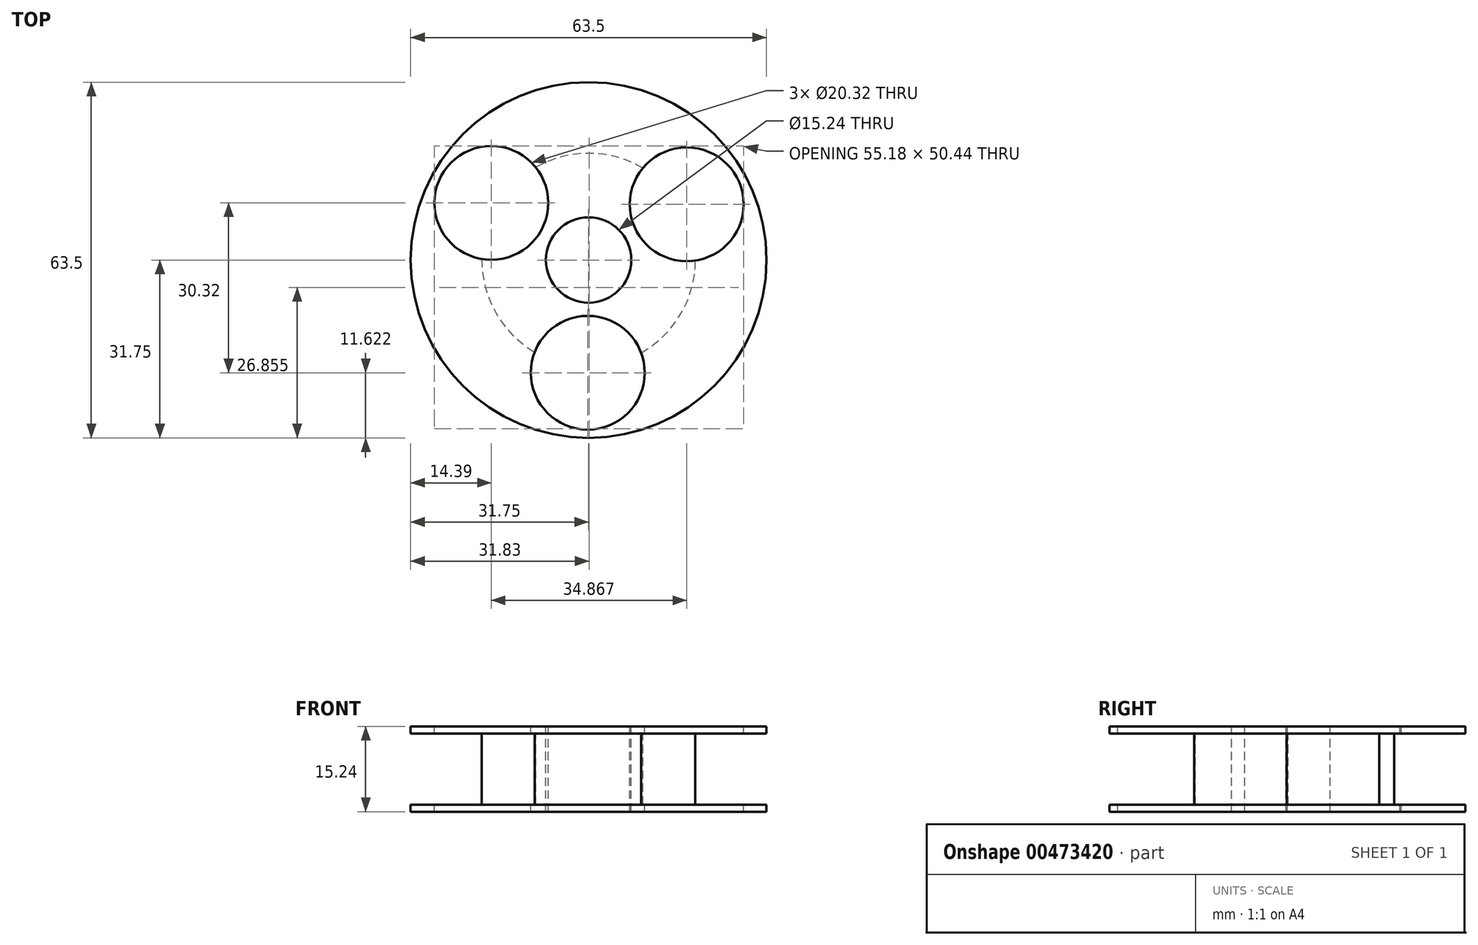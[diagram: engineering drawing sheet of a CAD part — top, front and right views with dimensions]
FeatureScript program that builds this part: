
annotation { "Feature Type Name" : "Feature", "Feature Type Description" : "" }
export const myFeature = defineFeature(function(context is Context, id is Id, definition is map)
    precondition{}
    {
        {
            var Q0;
            Q0=qCreatedBy(makeId("Top.planeOp"),FACE);
            var sketch = newSketch(context, id + "F0", { "sketchPlane" : qUnion([Q0])});
            skCircle(sketch, "E0", {"center": v(0, 0) * mm, "radius": 31.75 * mm});
            skSolve(sketch);
        }
        {
            var Q0;
            Q0=makeQuery(id+"F0.imprint","IMPRINT",FACE,{"disambiguationData":[TD([[makeQuery(id+"F0.imprint","IMPRINT",EDGE,{"derivedFrom":sQuery(id+"F0.wireOp",EDGE,"E0")}),1.0]])]});
            extrude(context, id + "F1", {"entities" : qUnion([Q0]), "depth" : 1.27 * mm});
        }
        {
            var Q0;
            Q0=makeQuery(id+"F1.opExtrude","CAP_FACE",FACE,{"disambiguationData":[OSD([sQuery(id+"F0.wireOp",EDGE,"E0")])],"isStart":false});
            var sketch = newSketch(context, id + "F2", { "sketchPlane" : qUnion([Q0])});
            skCircle(sketch, "E1", {"center": v(0, 0) * mm, "radius": 19.05 * mm});
            skSolve(sketch);
        }
        {
            var Q0;
            Q0=makeQuery(id+"F2.imprint","IMPRINT",FACE,{"disambiguationData":[TD([[makeQuery(id+"F2.imprint","IMPRINT",EDGE,{"derivedFrom":sQuery(id+"F2.wireOp",EDGE,"E1")}),1.0]])]});
            extrude(context, id + "F3", {"entities" : qUnion([Q0]), "operationType" : NewBodyOperationType.ADD, "depth" : 12.7 * mm});
        }
        {
            var Q0;
            Q0=makeQuery(id+"F3.opExtrude","CAP_FACE",FACE,{"disambiguationData":[OSD([sQuery(id+"F2.wireOp",EDGE,"E1")])],"isStart":false});
            var sketch = newSketch(context, id + "F4", { "sketchPlane" : qUnion([Q0])});
            skCircle(sketch, "E2", {"center": v(0, 0) * mm, "radius": 31.75 * mm});
            skSolve(sketch);
        }
        {
            var Q0;
            Q0 = qSketchRegion(id + "F4", true);
            extrude(context, id + "F5", {"entities" : qUnion([Q0]), "operationType" : NewBodyOperationType.ADD, "depth" : 1.27 * mm});
        }
        {
            var Q0;
            Q0=makeQuery(id+"F5.opExtrude","CAP_FACE",FACE,{"disambiguationData":[OSD([sQuery(id+"F4.wireOp",EDGE,"E2")])],"isStart":false});
            var sketch = newSketch(context, id + "F6", { "sketchPlane" : qUnion([Q0])});
            skCircle(sketch, "E3.cCircle", {"center": v(0, 0) * mm, "radius": 31.75 * mm, "construction": true});
            skLineSegment(sketch, "E3.0", {"start": v(-27.38, 16.07) * mm, "end": v(0.23, 31.75) * mm});
            skLineSegment(sketch, "E3.1", {"start": v(0.23, 31.75) * mm, "end": v(27.61, 15.67) * mm});
            skLineSegment(sketch, "E3.2", {"start": v(27.61, 15.67) * mm, "end": v(27.38, -16.07) * mm});
            skLineSegment(sketch, "E3.3", {"start": v(27.38, -16.07) * mm, "end": v(-0.23, -31.75) * mm});
            skLineSegment(sketch, "E3.4", {"start": v(-0.23, -31.75) * mm, "end": v(-27.61, -15.67) * mm});
            skLineSegment(sketch, "E3.5", {"start": v(-27.61, -15.67) * mm, "end": v(-27.38, 16.07) * mm});
            skLineSegment(sketch, "E4", {"start": v(13.92, 23.71) * mm, "end": v(-13.92, -23.71) * mm});
            skLineSegment(sketch, "E5", {"start": v(27.5, -0.2) * mm, "end": v(-27.5, -0.2) * mm});
            skLineSegment(sketch, "E6", {"start": v(13.57, -23.91) * mm, "end": v(-13.57, 23.91) * mm});
            skCircle(sketch, "E7.cCircle", {"center": v(0, 0) * mm, "radius": 17.22 * mm, "construction": true});
            skLineSegment(sketch, "E7.0", {"start": v(-8.5, 14.97) * mm, "end": v(8.72, 14.85) * mm});
            skLineSegment(sketch, "E7.1", {"start": v(8.72, 14.85) * mm, "end": v(17.22, -0.13) * mm});
            skLineSegment(sketch, "E7.2", {"start": v(17.22, -0.13) * mm, "end": v(8.5, -14.97) * mm});
            skLineSegment(sketch, "E7.3", {"start": v(8.5, -14.97) * mm, "end": v(-8.72, -14.85) * mm});
            skLineSegment(sketch, "E7.4", {"start": v(-8.72, -14.85) * mm, "end": v(-17.22, 0.13) * mm});
            skLineSegment(sketch, "E7.5", {"start": v(-17.22, 0.13) * mm, "end": v(-8.5, 14.97) * mm});
            skCircle(sketch, "E8", {"center": v(17.5, 9.94) * mm, "radius": 10.07 * mm});
            skPoint(sketch, "E8.third.point", {"position": v(22.27, 18.8) * mm});
            skCircle(sketch, "E9", {"center": v(-17.36, 10.2) * mm, "radius": 10.07 * mm});
            skPoint(sketch, "E9.third.point", {"position": v(-22.59, 18.8) * mm});
            skCircle(sketch, "E10", {"center": v(-0.15, -20.13) * mm, "radius": 10.07 * mm});
            skPoint(sketch, "E10.third.point", {"position": v(-5.43, -28.7) * mm});
            skSolve(sketch);
        }
        {
            var Q0;
            Q0=sQuery(id+"F6.wireOp",VERTEX,"E8.center");
            var Q1;
            Q1=makeQuery(id+"F1.opExtrude","SWEPT_BODY",BODY,{"disambiguationData":[OSD([sQuery(id+"F0.wireOp",EDGE,"E0")])]});
            hole(context, id + "F7", {"style" : HoleStyle.SIMPLE, "endStyle" : HoleEndStyle.THROUGH, "holeDiameter" : 20.32 * mm, "isTappedThrough" : true, "tappedDepth" : 12.7 * mm, "tapClearance" : 3, "locations" : qUnion([Q0]), "scope" : qUnion([Q1])});
        }
        {
            var Q0;
            Q0=sQuery(id+"F6.wireOp",VERTEX,"E10.center");
            var Q1;
            Q1=makeQuery(id+"F1.opExtrude","SWEPT_BODY",BODY,{"disambiguationData":[OSD([sQuery(id+"F0.wireOp",EDGE,"E0")])]});
            hole(context, id + "F8", {"style" : HoleStyle.SIMPLE, "endStyle" : HoleEndStyle.THROUGH, "holeDiameter" : 20.32 * mm, "isTappedThrough" : true, "tappedDepth" : 12.7 * mm, "tapClearance" : 3, "locations" : qUnion([Q0]), "scope" : qUnion([Q1])});
        }
        {
            var Q0;
            Q0=sQuery(id+"F6.wireOp",VERTEX,"E9.center");
            var Q1;
            Q1=makeQuery(id+"F1.opExtrude","SWEPT_BODY",BODY,{"disambiguationData":[OSD([sQuery(id+"F0.wireOp",EDGE,"E0")])]});
            hole(context, id + "F9", {"style" : HoleStyle.SIMPLE, "endStyle" : HoleEndStyle.THROUGH, "holeDiameter" : 20.32 * mm, "isTappedThrough" : true, "tappedDepth" : 12.7 * mm, "tapClearance" : 3, "locations" : qUnion([Q0]), "scope" : qUnion([Q1])});
        }
        {
            var Q0;
            Q0=makeQuery(id+"F5.opExtrude","CAP_FACE",FACE,{"disambiguationData":[OSD([sQuery(id+"F4.wireOp",EDGE,"E2")])],"isStart":false});
            var sketch = newSketch(context, id + "F10", { "sketchPlane" : qUnion([Q0])});
            skCircle(sketch, "E11", {"center": v(0, 0) * mm, "radius": 6.95 * mm});
            skSolve(sketch);
        }
        {
            var Q0;
            Q0=sQuery(id+"F10.wireOp",VERTEX,"E11.center");
            var Q1;
            Q1=makeQuery(id+"F1.opExtrude","SWEPT_BODY",BODY,{"disambiguationData":[OSD([sQuery(id+"F0.wireOp",EDGE,"E0")])]});
            hole(context, id + "F11", {"style" : HoleStyle.SIMPLE, "endStyle" : HoleEndStyle.THROUGH, "holeDiameter" : 15.24 * mm, "isTappedThrough" : true, "tappedDepth" : 12.7 * mm, "tapClearance" : 3, "locations" : qUnion([Q0]), "scope" : qUnion([Q1])});
        }
    });
